# Revit family: DHE (mm)
name_source: partatom
category: Electrical Equipment
revit_build: Autodesk Revit 2018 (Build: 20180329_1100(x64)
units: mm (PartAtom-declared; Revit-internal decimal feet)

## family parameters
Always vertical = No
Cut with Voids When Loaded = No
OmniClass Number = 23.31.29.11.11
OmniClass Title = Electric Instantaneous Hot Water Heaters
Part Type = Other Panel
Room Calculation Point = No
Round Connector Dimension = Use Diameter
Shared = No
Work Plane-Based = Yes

## types (2) — shared parameters
Color = White
Construction = pressure
Default Elevation = 1219 mm
Depth = 116 mm
Edition number = 1
Electrical connection = 3/P
Energy efficiency class = A
Heating system = Bare wire
Height = 466 mm
IP rating = IP 25
Manufacturer = Stiebel Eltron Gesellschaft m.b.H.
Manufacturer name = Stiebel Eltron GmbH
Material Black Plastic = Stiebel Eltron - Plastic - Black
Material Cover = Stiebel Eltron - Plastic - White
Material Transparent Plastic = Stiebel Eltron - Plastic - Transparent Grey
Nominal overpressure = 1 MPa (10)
Pipe outside diameter cold drinking water = 22 mm
Pipe outside diameter of warm drinking water = 22 mm
Product Guid = e7fc9edc-0f33-4311-b036-0cbfa60fea5f
Product SKU = dhe
Product data url = https://bimobject.com
Product name = DHE
QR code = https://bimobject.com
Switch-on quantity = 2,5
Temperature selection = Off, 20–60 °C
Type of scheme = electronic
URL = https://www.stiebel-eltron.de
Water connection = G 1/2
Weight = 3,10 kg
Width = 225 mm
nominal capacity = 0.4l
Δ ϕ on delivery = 28K

## per-type parameters (varying)
| type | Domestic hot water delivery | Frequency | Fuse protection | Model | Rated current | Rated output |
| Type - (DHE 202656) Power - (18/21/24 kW) | 9,2/10,7/12,3 l/min | 50/60 Hz | 32/32/35 A | DHE 18/21/24 | 29/31/35 A | 18/21/24 kW |
| Type - (DHE 202657) Power - (27 kW) | 13,8 l/min | 50/- Hz | 40 A | DHE 27 | 39 A | 27 kW |

## geometry (parser evidence)
native form markers: Sweep x2
no freeform markers — native parametric forms only
